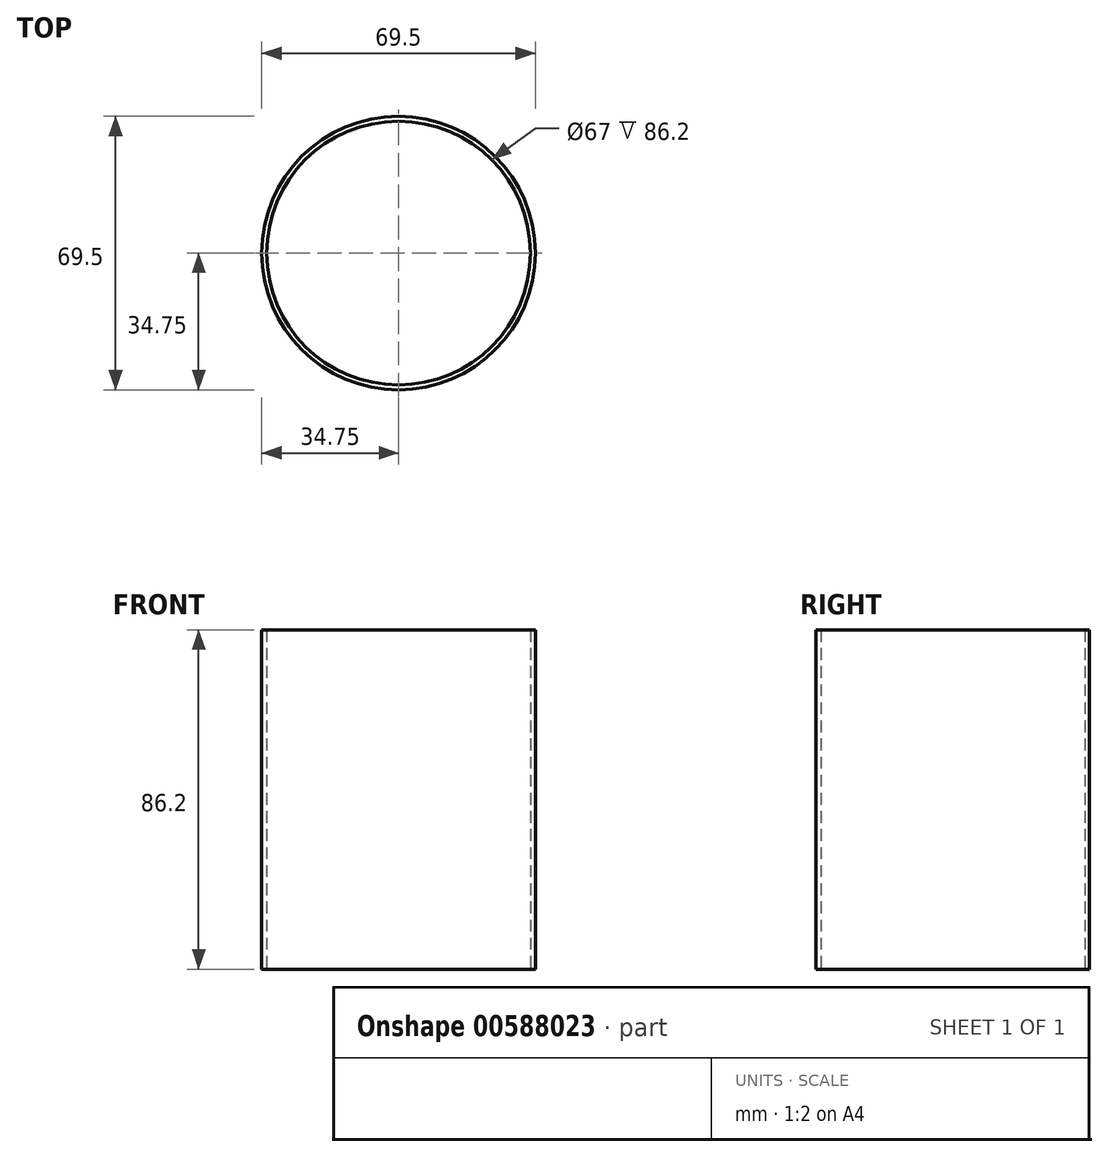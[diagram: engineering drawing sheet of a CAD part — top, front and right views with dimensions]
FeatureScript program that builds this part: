
annotation { "Feature Type Name" : "Feature", "Feature Type Description" : "" }
export const myFeature = defineFeature(function(context is Context, id is Id, definition is map)
    precondition{}
    {
        {
            assignVariable(context, id + "F0", {"name" : "ref_height", "anyValue" : 81.2});
        }
        {
            assignVariable(context, id + "F1", {"name" : "height", "anyValue" : getVariable(context, 'ref_height') + 5});
        }
        {
            var Q0;
            Q0=qCreatedBy(makeId("Top.planeOp"),FACE);
            var sketch = newSketch(context, id + "F2", { "sketchPlane" : qUnion([Q0])});
            skCircle(sketch, "E0", {"center": v(0, 0) * mm, "radius": 34.75 * mm});
            skCircle(sketch, "E1", {"center": v(0, 0) * mm, "radius": 33.5 * mm});
            skSolve(sketch);
        }
        {
            var Q0;
            Q0=makeQuery(id+"F2.imprint","IMPRINT",FACE,{"disambiguationData":[TD([[makeQuery(id+"F2.imprint","IMPRINT",EDGE,{"derivedFrom":sQuery(id+"F2.wireOp",EDGE,"E0")}),1.0]])]});
            extrude(context, id + "F3", {"entities" : qUnion([Q0]), "depth" : (getVariable(context, 'height')) * mm, "offsetDistance" : 25 * mm});
        }
    });
